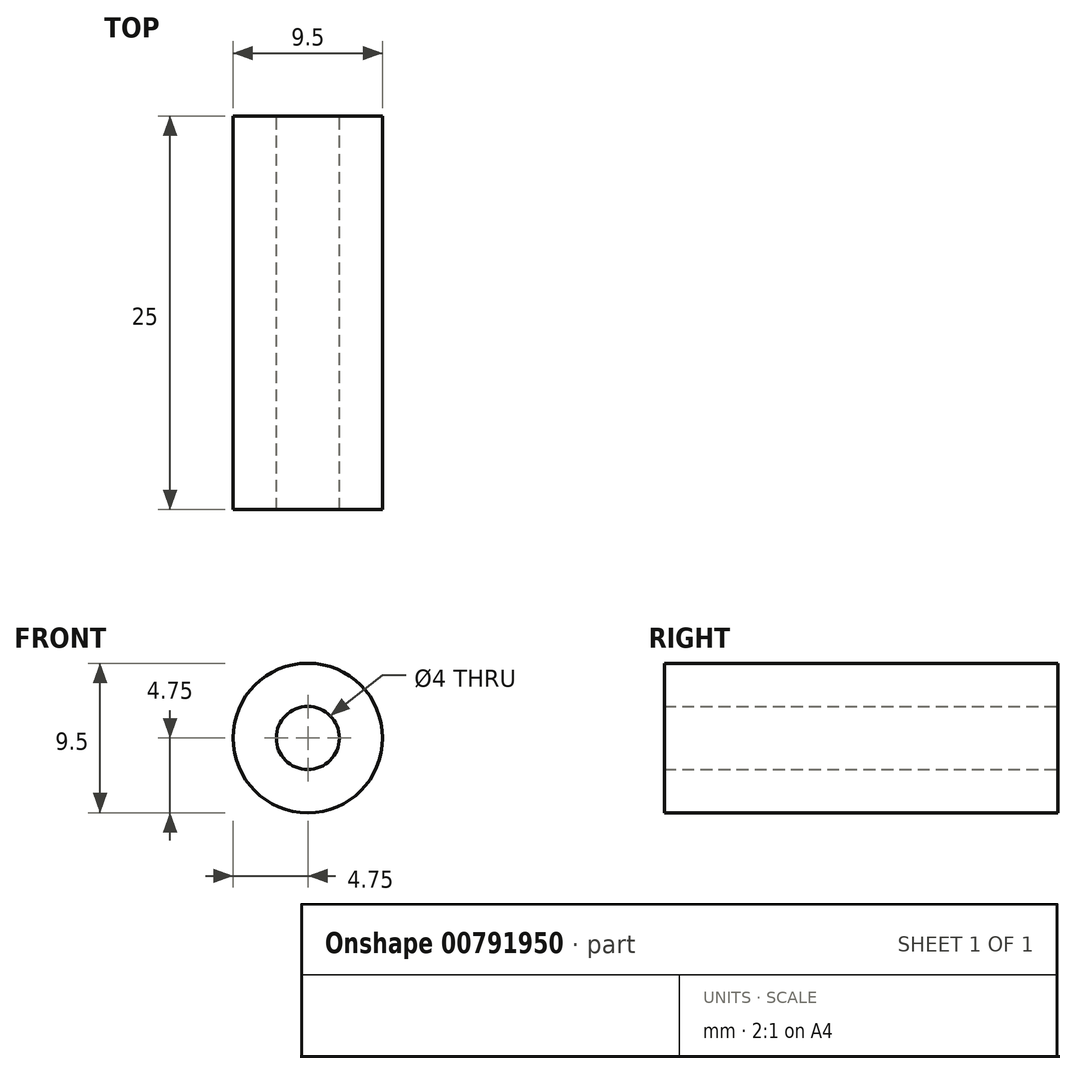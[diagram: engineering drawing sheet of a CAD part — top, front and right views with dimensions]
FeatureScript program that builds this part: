
annotation { "Feature Type Name" : "Feature", "Feature Type Description" : "" }
export const myFeature = defineFeature(function(context is Context, id is Id, definition is map)
    precondition{}
    {
        {
            var Q0;
            Q0=qCreatedBy(makeId("Front.planeOp"),FACE);
            var sketch = newSketch(context, id + "F0", { "sketchPlane" : qUnion([Q0])});
            skCircle(sketch, "E0", {"center": v(0, 0) * mm, "radius": 2 * mm});
            skCircle(sketch, "E1", {"center": v(0, 0) * mm, "radius": 4.75 * mm});
            skSolve(sketch);
        }
        {
            var Q0;
            Q0 = qSketchRegion(id + "F0", true);
            extrude(context, id + "F1", {"entities" : qUnion([Q0]), "depth" : 25 * mm, "offsetDistance" : 25 * mm});
        }
    });
